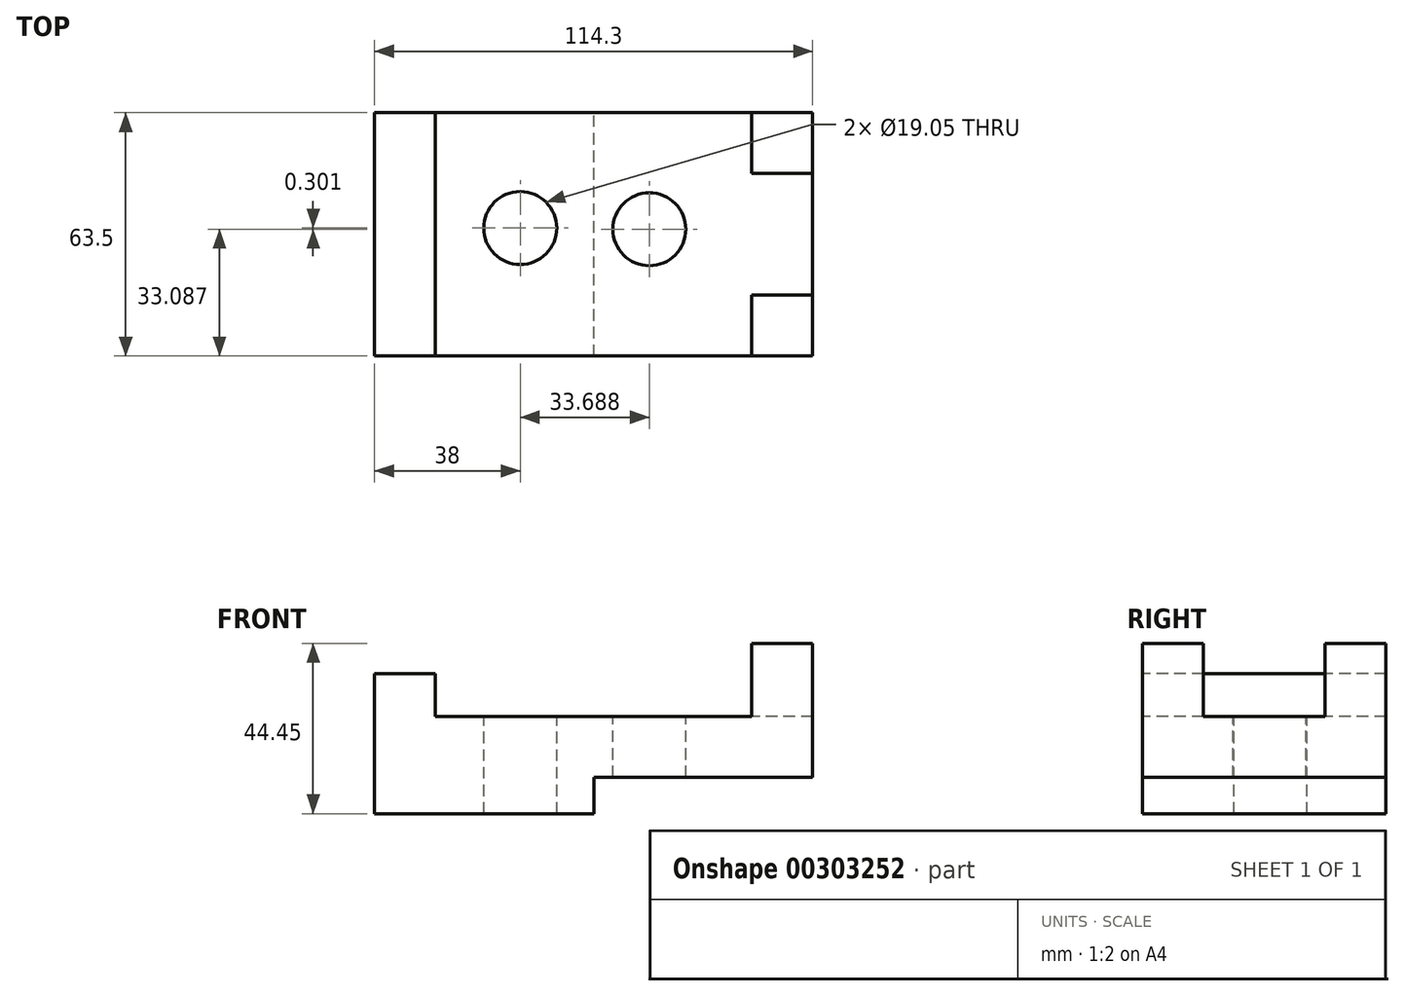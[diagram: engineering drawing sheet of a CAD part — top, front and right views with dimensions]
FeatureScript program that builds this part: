
annotation { "Feature Type Name" : "Feature", "Feature Type Description" : "" }
export const myFeature = defineFeature(function(context is Context, id is Id, definition is map)
    precondition{}
    {
        {
            var Q0;
            Q0=qCreatedBy(makeId("Top.planeOp"),FACE);
            var sketch = newSketch(context, id + "F0", { "sketchPlane" : qUnion([Q0])});
            skLineSegment(sketch, "E0.bottom", {"start": v(0, 0) * mm, "end": v(114.3, 0) * mm});
            skLineSegment(sketch, "E0.top", {"start": v(0, 63.5) * mm, "end": v(114.3, 63.5) * mm});
            skLineSegment(sketch, "E0.left", {"start": v(0, 0) * mm, "end": v(0, 63.5) * mm});
            skLineSegment(sketch, "E0.right", {"start": v(114.3, 0) * mm, "end": v(114.3, 63.5) * mm});
            skSolve(sketch);
        }
        {
            var Q0;
            Q0 = qSketchRegion(id + "F0", true);
            extrude(context, id + "F1", {"entities" : qUnion([Q0]), "depth" : 36.5 * mm});
        }
        {
            var Q0;
            Q0=makeQuery(id+"F1.opExtrude","CAP_FACE",FACE,{"disambiguationData":[OSD([sQuery(id+"F0.wireOp",EDGE,"E0.bottom"),sQuery(id+"F0.wireOp",EDGE,"E0.top"),sQuery(id+"F0.wireOp",EDGE,"E0.left"),sQuery(id+"F0.wireOp",EDGE,"E0.right")])],"isStart":false});
            var sketch = newSketch(context, id + "F2", { "sketchPlane" : qUnion([Q0])});
            skLineSegment(sketch, "E1.bottom", {"start": v(0, 0) * mm, "end": v(114.3, 0) * mm});
            skLineSegment(sketch, "E1.top", {"start": v(0, 63.5) * mm, "end": v(114.3, 63.5) * mm});
            skLineSegment(sketch, "E1.left", {"start": v(0, 0) * mm, "end": v(0, 63.5) * mm});
            skLineSegment(sketch, "E1.right", {"start": v(114.3, 0) * mm, "end": v(114.3, 63.5) * mm});
            skSolve(sketch);
        }
        {
            var Q0;
            Q0=makeQuery(id+"F2.imprint","IMPRINT",FACE,{"disambiguationData":[TD([[makeQuery(id+"F2.imprint","IMPRINT",EDGE,{"derivedFrom":sQuery(id+"F2.wireOp",EDGE,"E1.bottom")}),1.0]])]});
            extrude(context, id + "F3", {"entities" : qUnion([Q0]), "operationType" : NewBodyOperationType.REMOVE, "oppositeDirection" : true, "depth" : 11.1 * mm});
        }
        {
            var Q0;
            Q0=qCreatedBy(makeId("Top.planeOp"),FACE);
            var sketch = newSketch(context, id + "F4", { "sketchPlane" : qUnion([Q0])});
            skLineSegment(sketch, "E2.bottom", {"start": v(114.4, 0) * mm, "end": v(57.25, 0) * mm});
            skLineSegment(sketch, "E2.top", {"start": v(114.4, 64.07) * mm, "end": v(57.25, 64.07) * mm});
            skLineSegment(sketch, "E2.left", {"start": v(114.4, 0) * mm, "end": v(114.4, 64.07) * mm});
            skLineSegment(sketch, "E2.right", {"start": v(57.25, 0) * mm, "end": v(57.25, 64.07) * mm});
            skSolve(sketch);
        }
        {
            var Q0;
            Q0=makeQuery(id+"F4.imprint","IMPRINT",FACE,{"disambiguationData":[TD([[makeQuery(id+"F4.imprint","IMPRINT",EDGE,{"derivedFrom":sQuery(id+"F4.wireOp",EDGE,"E2.bottom")}),-1.0]])]});
            extrude(context, id + "F5", {"entities" : qUnion([Q0]), "operationType" : NewBodyOperationType.REMOVE, "depth" : 9.52 * mm});
        }
        {
            var Q0;
            Q0=makeQuery(id+"F3.boolean.opBoolean","COPY",FACE,{"derivedFrom":makeQuery(id+"F3.opExtrude","CAP_FACE",FACE,{"disambiguationData":[OSD([sQuery(id+"F2.wireOp",EDGE,"E1.bottom"),sQuery(id+"F2.wireOp",EDGE,"E1.top"),sQuery(id+"F2.wireOp",EDGE,"E1.left"),sQuery(id+"F2.wireOp",EDGE,"E1.right")])],"isStart":false})});
            var sketch = newSketch(context, id + "F6", { "sketchPlane" : qUnion([Q0])});
            skLineSegment(sketch, "E3.bottom", {"start": v(114.3, 0) * mm, "end": v(98.43, 0) * mm});
            skLineSegment(sketch, "E3.top", {"start": v(114.3, 15.88) * mm, "end": v(98.43, 15.88) * mm});
            skLineSegment(sketch, "E3.left", {"start": v(114.3, 0) * mm, "end": v(114.3, 15.88) * mm});
            skLineSegment(sketch, "E3.right", {"start": v(98.43, 0) * mm, "end": v(98.43, 15.88) * mm});
            skSolve(sketch);
        }
        {
            var Q0;
            Q0=makeQuery(id+"F6.imprint","IMPRINT",FACE,{"disambiguationData":[TD([[makeQuery(id+"F6.imprint","IMPRINT",EDGE,{"derivedFrom":sQuery(id+"F6.wireOp",EDGE,"E3.bottom")}),1.0]])]});
            extrude(context, id + "F7", {"entities" : qUnion([Q0]), "operationType" : NewBodyOperationType.ADD, "depth" : 19.05 * mm});
        }
        {
            var Q0;
            Q0=makeQuery(id+"F3.boolean.opBoolean","COPY",FACE,{"derivedFrom":makeQuery(id+"F3.opExtrude","CAP_FACE",FACE,{"disambiguationData":[OSD([sQuery(id+"F2.wireOp",EDGE,"E1.bottom"),sQuery(id+"F2.wireOp",EDGE,"E1.top"),sQuery(id+"F2.wireOp",EDGE,"E1.left"),sQuery(id+"F2.wireOp",EDGE,"E1.right")])],"isStart":false})});
            var sketch = newSketch(context, id + "F8", { "sketchPlane" : qUnion([Q0])});
            skLineSegment(sketch, "E4.bottom", {"start": v(114.3, 63.5) * mm, "end": v(98.43, 63.5) * mm});
            skLineSegment(sketch, "E4.top", {"start": v(114.3, 47.63) * mm, "end": v(98.43, 47.63) * mm});
            skLineSegment(sketch, "E4.left", {"start": v(114.3, 63.5) * mm, "end": v(114.3, 47.63) * mm});
            skLineSegment(sketch, "E4.right", {"start": v(98.43, 63.5) * mm, "end": v(98.43, 47.63) * mm});
            skSolve(sketch);
        }
        {
            var Q0;
            Q0 = qSketchRegion(id + "F8", true);
            extrude(context, id + "F9", {"entities" : qUnion([Q0]), "operationType" : NewBodyOperationType.ADD, "depth" : 19.05 * mm});
        }
        {
            var Q0;
            Q0=makeQuery(id+"F3.boolean.opBoolean","COPY",FACE,{"derivedFrom":makeQuery(id+"F3.opExtrude","CAP_FACE",FACE,{"disambiguationData":[OSD([sQuery(id+"F2.wireOp",EDGE,"E1.bottom"),sQuery(id+"F2.wireOp",EDGE,"E1.top"),sQuery(id+"F2.wireOp",EDGE,"E1.left"),sQuery(id+"F2.wireOp",EDGE,"E1.right")])],"isStart":false})});
            var sketch = newSketch(context, id + "F10", { "sketchPlane" : qUnion([Q0])});
            skLineSegment(sketch, "E5.bottom", {"start": v(0, 63.5) * mm, "end": v(15.88, 63.5) * mm});
            skLineSegment(sketch, "E5.top", {"start": v(0, 0) * mm, "end": v(15.88, 0) * mm});
            skLineSegment(sketch, "E5.left", {"start": v(0, 63.5) * mm, "end": v(0, 0) * mm});
            skLineSegment(sketch, "E5.right", {"start": v(15.88, 63.5) * mm, "end": v(15.88, 0) * mm});
            skSolve(sketch);
        }
        {
            var Q0;
            Q0 = qSketchRegion(id + "F10", true);
            extrude(context, id + "F11", {"entities" : qUnion([Q0]), "operationType" : NewBodyOperationType.ADD, "depth" : 11.1 * mm});
        }
        {
            var Q0;
            Q0=makeQuery(id+"F3.boolean.opBoolean","COPY",FACE,{"derivedFrom":makeQuery(id+"F3.opExtrude","CAP_FACE",FACE,{"disambiguationData":[OSD([sQuery(id+"F2.wireOp",EDGE,"E1.bottom"),sQuery(id+"F2.wireOp",EDGE,"E1.top"),sQuery(id+"F2.wireOp",EDGE,"E1.left"),sQuery(id+"F2.wireOp",EDGE,"E1.right")])],"isStart":false})});
            var sketch = newSketch(context, id + "F12", { "sketchPlane" : qUnion([Q0])});
            skCircle(sketch, "E6", {"center": v(38, 33.39) * mm, "radius": 9.53 * mm});
            skSolve(sketch);
        }
        {
            var Q0;
            Q0=makeQuery(id+"F12.imprint","IMPRINT",FACE,{"disambiguationData":[TD([[makeQuery(id+"F12.imprint","IMPRINT",EDGE,{"derivedFrom":sQuery(id+"F12.wireOp",EDGE,"E6")}),1.0]])]});
            extrude(context, id + "F13", {"entities" : qUnion([Q0]), "operationType" : NewBodyOperationType.REMOVE, "oppositeDirection" : true, "depth" : 25.4 * mm});
        }
        {
            var Q0;
            Q0=makeQuery(id+"F3.boolean.opBoolean","COPY",FACE,{"derivedFrom":makeQuery(id+"F3.opExtrude","CAP_FACE",FACE,{"disambiguationData":[OSD([sQuery(id+"F2.wireOp",EDGE,"E1.bottom"),sQuery(id+"F2.wireOp",EDGE,"E1.top"),sQuery(id+"F2.wireOp",EDGE,"E1.left"),sQuery(id+"F2.wireOp",EDGE,"E1.right")])],"isStart":false})});
            var sketch = newSketch(context, id + "F14", { "sketchPlane" : qUnion([Q0])});
            skCircle(sketch, "E7", {"center": v(71.69, 33.09) * mm, "radius": 9.53 * mm});
            skSolve(sketch);
        }
        {
            var Q0;
            Q0=makeQuery(id+"F14.imprint","IMPRINT",FACE,{"disambiguationData":[TD([[makeQuery(id+"F14.imprint","IMPRINT",EDGE,{"derivedFrom":sQuery(id+"F14.wireOp",EDGE,"E7")}),1.0]])]});
            extrude(context, id + "F15", {"entities" : qUnion([Q0]), "operationType" : NewBodyOperationType.REMOVE, "oppositeDirection" : true, "depth" : 25.4 * mm});
        }
    });
